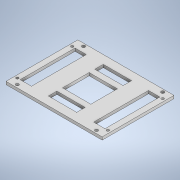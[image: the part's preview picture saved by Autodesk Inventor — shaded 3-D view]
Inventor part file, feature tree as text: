
AUTODESK INVENTOR PART (.ipt)
format: ipt  version: 2020 (Build 240168000, 168)  size: 187,904 bytes
history: native  units: mm
features: sketch x4, extrude x2, hole x2, other x1, projected_geometry x1
ambient origin geometry x8: Origin, YZ Plane, XZ Plane, XY Plane, X Axis, Y Axis, Z Axis, Center Point
bodies: Body1 (feature_tree)
feature tree (10):
  other  "솔리드1"
  extrude  "돌출1"  Depth=140.0mm
  hole  "구멍1"  [1 undecoded]
  extrude  "돌출2"  Depth=170.0mm
  hole  "구멍2"  [1 undecoded]
  sketch  "스케치1"
  sketch  "스케치2"
  sketch  "스케치3"
  sketch  "스케치4"
  projected_geometry  "투영된 루프1"
note: 2 required parameter values undecoded (feature->parameter linkage not recoverable at this tier; creation-order binding heuristic only, values carry confidence <= 0.55)
